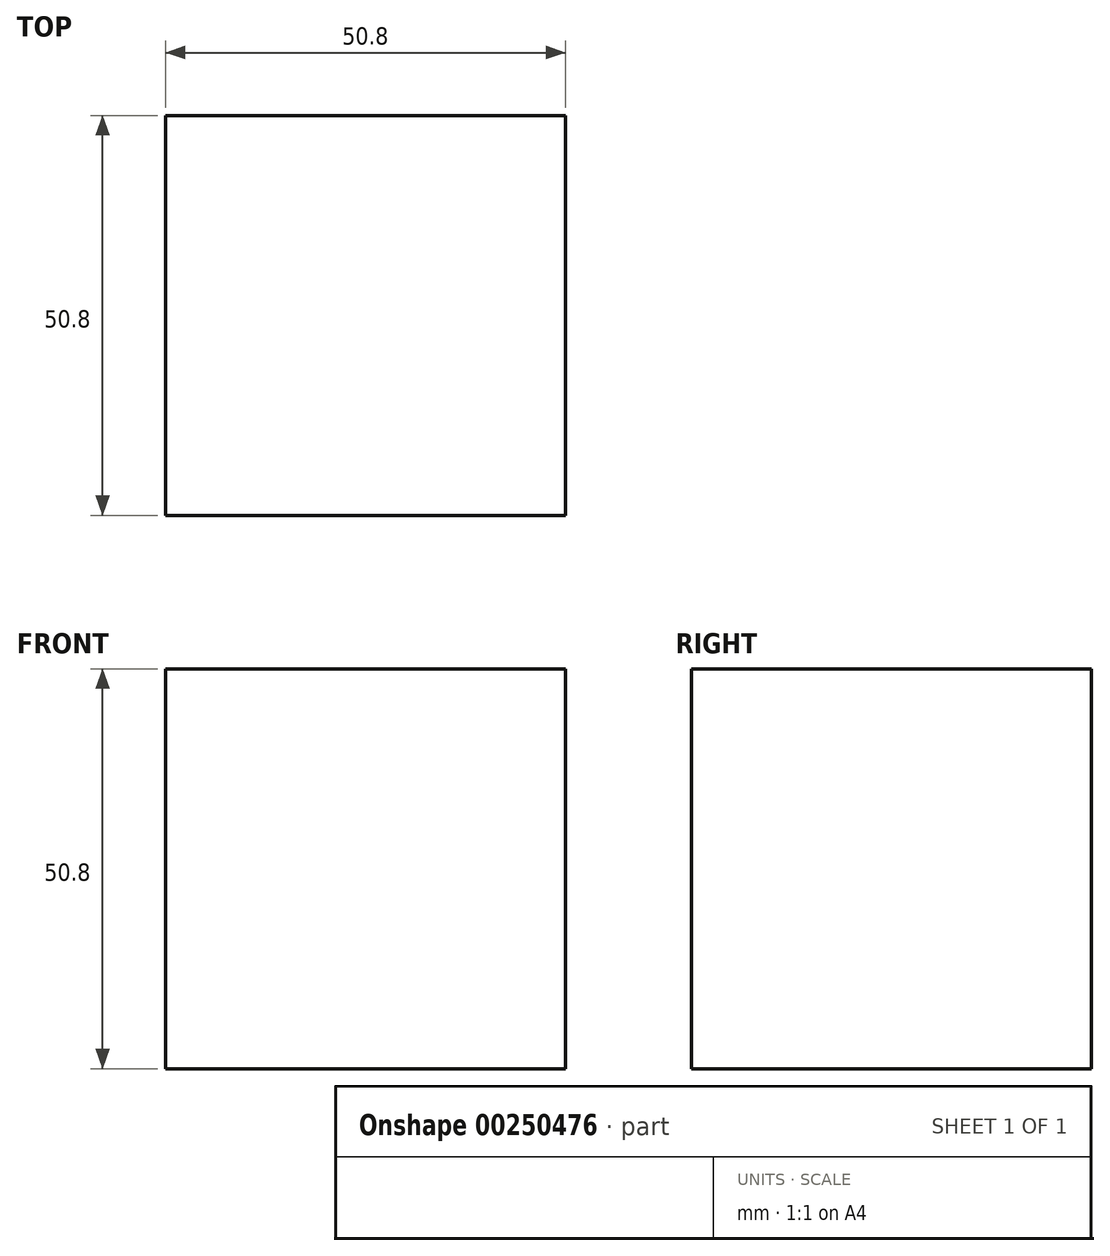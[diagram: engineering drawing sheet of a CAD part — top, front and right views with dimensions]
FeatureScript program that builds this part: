
annotation { "Feature Type Name" : "Feature", "Feature Type Description" : "" }
export const myFeature = defineFeature(function(context is Context, id is Id, definition is map)
    precondition{}
    {
        {
            var Q0;
            Q0=qCreatedBy(makeId("Front.planeOp"),FACE);
            var sketch = newSketch(context, id + "F0", { "sketchPlane" : qUnion([Q0])});
            skLineSegment(sketch, "E0.bottom", {"start": v(-25.4, 25.4) * mm, "end": v(25.4, 25.4) * mm});
            skLineSegment(sketch, "E0.top", {"start": v(-25.4, -25.4) * mm, "end": v(25.4, -25.4) * mm});
            skLineSegment(sketch, "E0.left", {"start": v(-25.4, 25.4) * mm, "end": v(-25.4, -25.4) * mm});
            skLineSegment(sketch, "E0.right", {"start": v(25.4, 25.4) * mm, "end": v(25.4, -25.4) * mm});
            skPoint(sketch, "E0.middle", {"position": v(0, 0) * mm});
            skSolve(sketch);
        }
        {
            var Q0;
            Q0=makeQuery(id+"F0.imprint","IMPRINT",FACE,{"disambiguationData":[TD([[makeQuery(id+"F0.imprint","IMPRINT",EDGE,{"derivedFrom":sQuery(id+"F0.wireOp",EDGE,"E0.bottom")}),-1.0]])]});
            extrude(context, id + "F1", {"entities" : qUnion([Q0]), "endBound" : BoundingType.SYMMETRIC, "depth" : 50.8 * mm});
        }
    });
